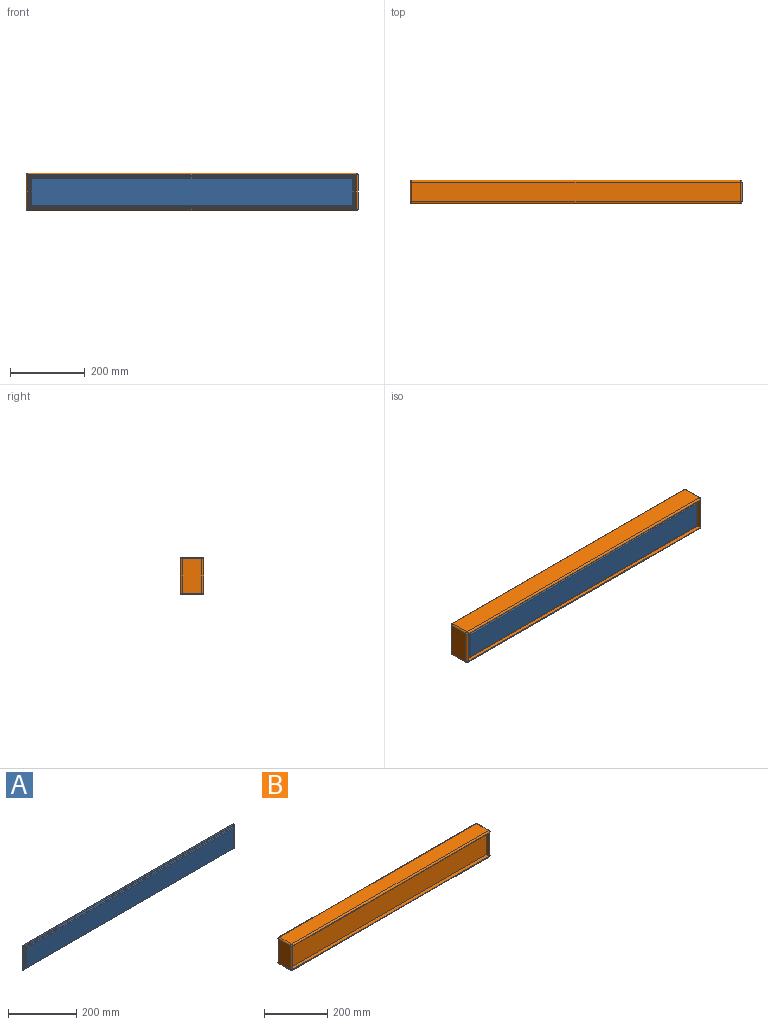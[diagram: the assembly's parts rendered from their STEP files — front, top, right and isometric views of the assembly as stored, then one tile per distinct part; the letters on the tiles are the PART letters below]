
ASSEMBLY  parts=2 mates=1
PART A: 23 faces, bbox 876.3x9.5x88.9 mm
  f0: plane 76.2x1.27mm, normal (-1,0,0), area 96.8mm2, adj f1,f3,f13,f19
  f1: plane 863.6x1.27mm, normal (0,0,-1), area 1096.8mm2, adj f0,f2,f11,f20
  f2: plane 76.2x1.27mm, normal (1,0,0), area 96.8mm2, adj f1,f3,f12,f22
  f3: plane 863.6x1.27mm, normal (0,0,1), area 1096.8mm2, adj f0,f2,f14,f21
  f4: plane 858.52x71.12mm, normal (0,-1,0), area 61057.9mm2, adj f19,f20,f21,f22
  f5: plane 88.9x0.64mm, normal (1,0,0), area 56.5mm2, adj f6,f8,f10,f16
  f6: plane 876.3x0.64mm, normal (0,0,1), area 556.5mm2, adj f5,f7,f10,f15
  f7: plane 88.9x0.64mm, normal (-1,0,0), area 56.5mm2, adj f6,f8,f10,f17
  f8: plane 876.3x0.64mm, normal (0,0,-1), area 556.5mm2, adj f5,f7,f10,f18
  f9: plane 871.22x83.82mm, normal (0,-1,0), area 2419.3mm2, adj f11,f12,f13,f14,f15,f16,f17,f18
  f10: plane 876.3x88.9mm, normal (0,1,0), area 77903.1mm2, adj f5,f6,f7,f8
  f11: cylinder r=2.54mm len=868.68mm, axis (1,0,0), area 3453mm2, adj f1,f9,f12,f13
  f12: cylinder r=2.54mm len=81.28mm, axis (0,0,1), area 311.4mm2, adj f2,f9,f11,f14
  f13: cylinder r=2.54mm len=81.28mm, axis (0,0,-1), area 311.4mm2, adj f0,f9,f11,f14
  f14: cylinder r=2.54mm len=868.68mm, axis (-1,0,0), area 3453mm2, adj f3,f9,f12,f13
  f15: cylinder r=2.54mm len=876.3mm, axis (1,0,0), area 3488.9mm2, adj f6,f9,f16,f17
  f16: cylinder r=2.54mm len=88.9mm, axis (0,0,-1), area 347.3mm2, adj f5,f9,f15,f18
  f17: cylinder r=2.54mm len=88.9mm, axis (0,0,1), area 347.3mm2, adj f7,f9,f15,f18
  f18: cylinder r=2.54mm len=876.3mm, axis (-1,0,0), area 3488.9mm2, adj f8,f9,f16,f17
  f19: cylinder r=2.54mm len=76.2mm, axis (0,0,1), area 296.7mm2, adj f0,f4,f20,f21
  f20: cylinder r=2.54mm len=863.6mm, axis (-1,0,0), area 3438.2mm2, adj f1,f4,f19,f22
  f21: cylinder r=2.54mm len=863.6mm, axis (1,0,0), area 3438.2mm2, adj f3,f4,f19,f22
  f22: cylinder r=2.54mm len=76.2mm, axis (0,0,-1), area 296.7mm2, adj f2,f4,f20,f21
PART B: 36 faces, bbox 889x63.5x101.6 mm
  f0: plane 878.84x91.44mm, normal (0,-1,0), area 2458.1mm2, adj f11,f12,f13,f14,f19,f20,f29,f30
  f1: plane 878.84x91.44mm, normal (0,1,0), area 2458.1mm2, adj f6,f7,f8,f9,f22,f23,f31,f32
  f2: plane 91.44x53.34mm, normal (1,0,0), area 4877.4mm2, adj f24,f29,f32,f35
  f3: plane 878.84x53.34mm, normal (0,0,1), area 46877.3mm2, adj f21,f30,f31,f35
  f4: plane 91.44x53.34mm, normal (-1,0,0), area 4877.4mm2, adj f16,f20,f21,f22
  f5: plane 878.84x53.34mm, normal (0,0,-1), area 46877.3mm2, adj f16,f19,f23,f24
  f6: plane 88.9x12.7mm, normal (-1,0,0), area 1129mm2, adj f1,f7,f9,f10
  f7: plane 876.3x12.7mm, normal (0,0,-1), area 11129mm2, adj f1,f6,f8,f10
  f8: plane 88.9x12.7mm, normal (1,0,0), area 1129mm2, adj f1,f7,f9,f10
  f9: plane 876.3x12.7mm, normal (0,0,1), area 11129mm2, adj f1,f6,f8,f10
  f10: plane 876.3x88.9mm, normal (0,1,0), area 77903.1mm2, adj f6,f7,f8,f9
  f11: plane 88.9x12.7mm, normal (1,0,0), area 1129mm2, adj f0,f12,f14,f15
  f12: plane 876.3x12.7mm, normal (0,0,1), area 11129mm2, adj f0,f11,f13,f15
  f13: plane 88.9x12.7mm, normal (-1,0,0), area 1129mm2, adj f0,f12,f14,f15
  f14: plane 876.3x12.7mm, normal (0,0,-1), area 11129mm2, adj f0,f11,f13,f15
  f15: plane 876.3x88.9mm, normal (0,-1,0), area 77903.1mm2, adj f11,f12,f13,f14
  f16: cylinder r=5.08mm len=53.34mm, axis (0,1,0), area 425.6mm2, adj f4,f5,f17,f18
  f17: sphere r=5.08mm, area 40.5mm2, adj f16,f19,f20
  f18: sphere r=5.08mm, area 40.5mm2, adj f16,f22,f23
  f19: cylinder r=5.08mm len=878.84mm, axis (-1,0,0), area 7012.8mm2, adj f0,f5,f17,f25
  f20: cylinder r=5.08mm len=91.44mm, axis (0,0,1), area 729.7mm2, adj f0,f4,f17,f26
  f21: cylinder r=5.08mm len=53.34mm, axis (0,-1,0), area 425.6mm2, adj f3,f4,f26,f27
  f22: cylinder r=5.08mm len=91.44mm, axis (0,0,-1), area 729.7mm2, adj f1,f4,f18,f27
  f23: cylinder r=5.08mm len=878.84mm, axis (1,0,0), area 7012.8mm2, adj f1,f5,f18,f28
  f24: cylinder r=5.08mm len=53.34mm, axis (0,-1,0), area 425.6mm2, adj f2,f5,f25,f28
  f25: sphere r=5.08mm, area 40.5mm2, adj f19,f24,f29
  f26: sphere r=5.08mm, area 40.5mm2, adj f20,f21,f30
  f27: sphere r=5.08mm, area 40.5mm2, adj f21,f22,f31
  f28: sphere r=5.08mm, area 40.5mm2, adj f23,f24,f32
  f29: cylinder r=5.08mm len=91.44mm, axis (0,0,-1), area 729.7mm2, adj f0,f2,f25,f33
  f30: cylinder r=5.08mm len=878.84mm, axis (1,0,0), area 7012.8mm2, adj f0,f3,f26,f33
  f31: cylinder r=5.08mm len=878.84mm, axis (-1,0,0), area 7012.8mm2, adj f1,f3,f27,f34
  f32: cylinder r=5.08mm len=91.44mm, axis (0,0,1), area 729.7mm2, adj f1,f2,f28,f34
  f33: sphere r=5.08mm, area 40.5mm2, adj f29,f30,f35
  f34: sphere r=5.08mm, area 40.5mm2, adj f31,f32,f35
  f35: cylinder r=5.08mm len=53.34mm, axis (0,1,0), area 425.6mm2, adj f2,f3,f33,f34
PLACE A t=(-35.44,-141.23,-152.58)mm
PLACE B t=(-35.44,-90.43,-152.58)mm
MATE fastened A.f10 <-> B.f15  axis (0,1,0) through (-35.44,-141.23,-152.58)mm
